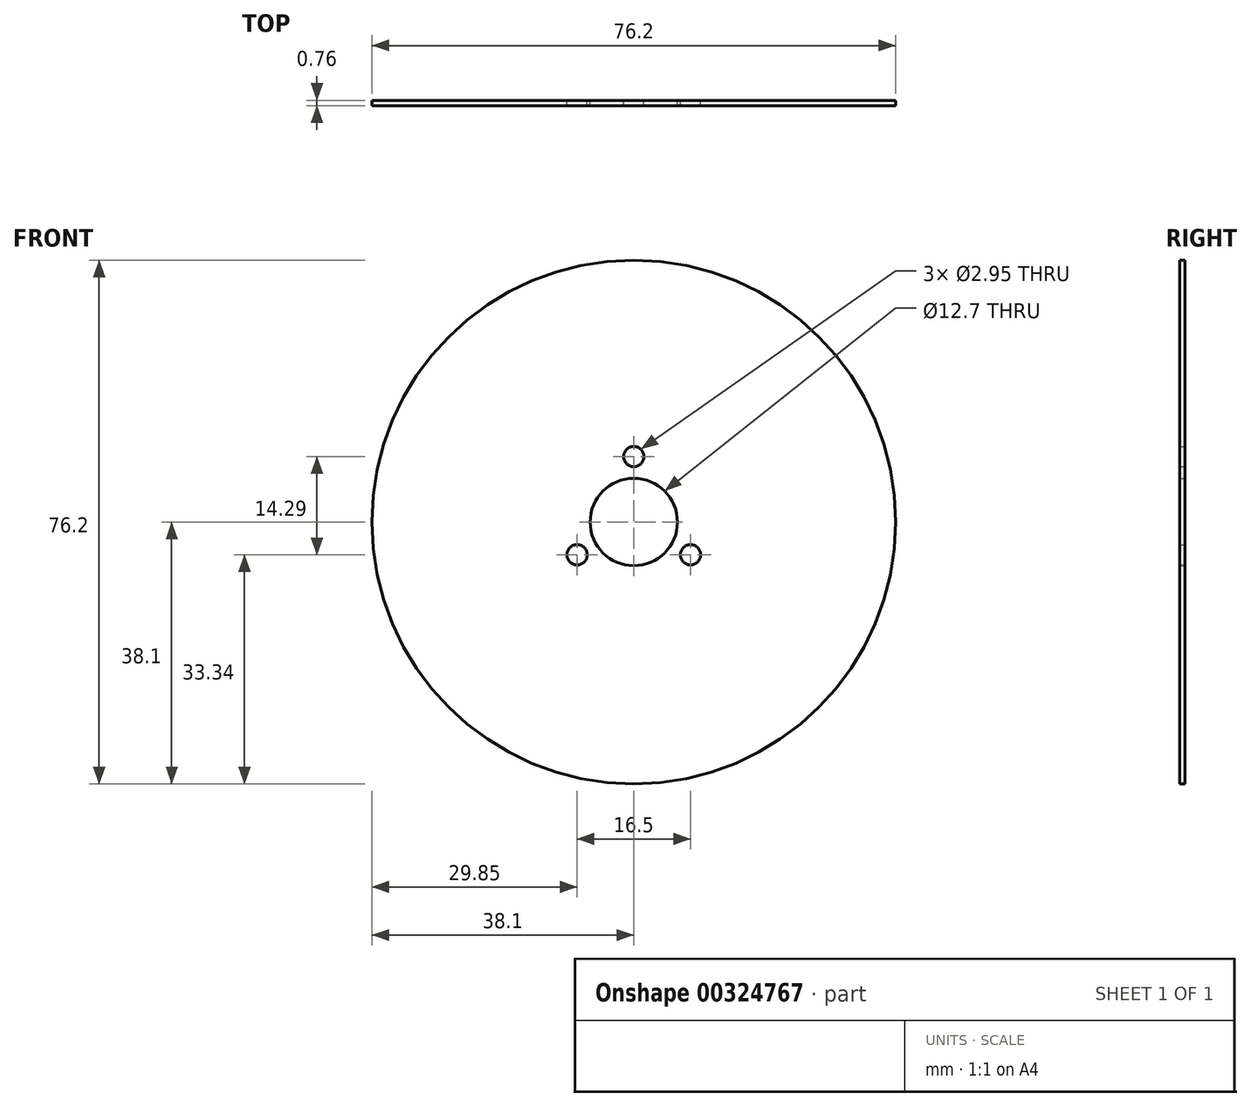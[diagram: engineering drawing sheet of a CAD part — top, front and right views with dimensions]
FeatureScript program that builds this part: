
annotation { "Feature Type Name" : "Feature", "Feature Type Description" : "" }
export const myFeature = defineFeature(function(context is Context, id is Id, definition is map)
    precondition{}
    {
        {
            var Q0;
            Q0=qCreatedBy(makeId("Front.planeOp"),FACE);
            var sketch = newSketch(context, id + "F0", { "sketchPlane" : qUnion([Q0])});
            skCircle(sketch, "E0", {"center": v(0, 0) * mm, "radius": 6.35 * mm});
            skCircle(sketch, "E1", {"center": v(0, 0) * mm, "radius": 38.1 * mm});
            skSolve(sketch);
        }
        {
            var Q0;
            Q0=makeQuery(id+"F0.imprint","IMPRINT",FACE,{"disambiguationData":[TD([[makeQuery(id+"F0.imprint","IMPRINT",EDGE,{"derivedFrom":sQuery(id+"F0.wireOp",EDGE,"E0")}),-1.0]])]});
            extrude(context, id + "F1", {"entities" : qUnion([Q0]), "depth" : 0.76 * mm, "offsetDistance" : 25.4 * mm});
        }
        {
            var Q0;
            Q0=makeQuery(id+"F1.opExtrude","CAP_FACE",FACE,{"disambiguationData":[OSD([sQuery(id+"F0.wireOp",EDGE,"E0"),sQuery(id+"F0.wireOp",EDGE,"E1")])],"isStart":false});
            var sketch = newSketch(context, id + "F2", { "sketchPlane" : qUnion([Q0])});
            skLineSegment(sketch, "E2", {"start": v(-0.93, 12.67) * mm, "end": v(-0.93, 38.09) * mm});
            skLineSegment(sketch, "E3.MirrorCS", {"start": v(0.93, 12.67) * mm, "end": v(0.93, 38.09) * mm});
            skArc(sketch, "E4", {"start": v(-0.93, 12.67) * mm, "mid": v(0, 12.7) * mm, "end": v(0.93, 12.67) * mm});
            skArc(sketch, "E5", {"start": v(-0.93, 38.09) * mm, "mid": v(0, 38.1) * mm, "end": v(0.93, 38.09) * mm});
            skLineSegment(sketch, "E6.anchor1", {"start": v(0, 0) * mm, "end": v(-0.93, 38.09) * mm, "construction": true});
            skLineSegment(sketch, "E6.anchor2", {"start": v(0, 0) * mm, "end": v(-0.93, 38.09) * mm, "construction": true});
            skSolve(sketch);
        }
        {
            var Q0;
            Q0=makeQuery(id+"F2.imprint","IMPRINT",FACE,{"disambiguationData":[TD([[makeQuery(id+"F2.imprint","IMPRINT",EDGE,{"derivedFrom":sQuery(id+"F2.wireOp",EDGE,"E5")}),1.0]])]});
            extrude(context, id + "F3", {"entities" : qUnion([Q0]), "operationType" : NewBodyOperationType.REMOVE, "endBound" : BoundingType.THROUGH_ALL, "oppositeDirection" : true, "depth" : 25.4 * mm, "offsetDistance" : 25.4 * mm});
        }
        {
            var Q0;
            Q0=makeQuery(id+"F1.opExtrude","CAP_FACE",FACE,{"disambiguationData":[OSD([sQuery(id+"F0.wireOp",EDGE,"E0"),sQuery(id+"F0.wireOp",EDGE,"E1")])],"isStart":false});
            var sketch = newSketch(context, id + "F4", { "sketchPlane" : qUnion([Q0])});
            skPoint(sketch, "E7", {"position": v(0, 9.53) * mm});
            skPoint(sketch, "E8.1.0", {"position": v(-8.25, -4.76) * mm});
            skPoint(sketch, "E8.2.0", {"position": v(8.25, -4.76) * mm});
            skPoint(sketch, "E8.center", {"position": v(0, 0) * mm});
            skSolve(sketch);
        }
        {
            var Q0;
            Q0=sQuery(id+"F4.wireOp",VERTEX,"E7");
            var Q1;
            Q1=sQuery(id+"F4.wireOp",VERTEX,"E8.1.0");
            var Q2;
            Q2=sQuery(id+"F4.wireOp",VERTEX,"E8.2.0");
            var Q3;
            Q3=makeQuery(id+"F1.opExtrude","SWEPT_BODY",BODY,{"disambiguationData":[OSD([sQuery(id+"F0.wireOp",EDGE,"E0"),sQuery(id+"F0.wireOp",EDGE,"E1")])]});
            hole(context, id + "F5", {"style" : HoleStyle.SIMPLE, "endStyle" : HoleEndStyle.THROUGH, "holeDiameter" : 2.95 * mm, "majorDiameter" : 6.35 * mm, "tappedDepth" : 12.7 * mm, "tapClearance" : 3, "locations" : qUnion([Q0, Q1, Q2]), "scope" : qUnion([Q3])});
        }
    });
